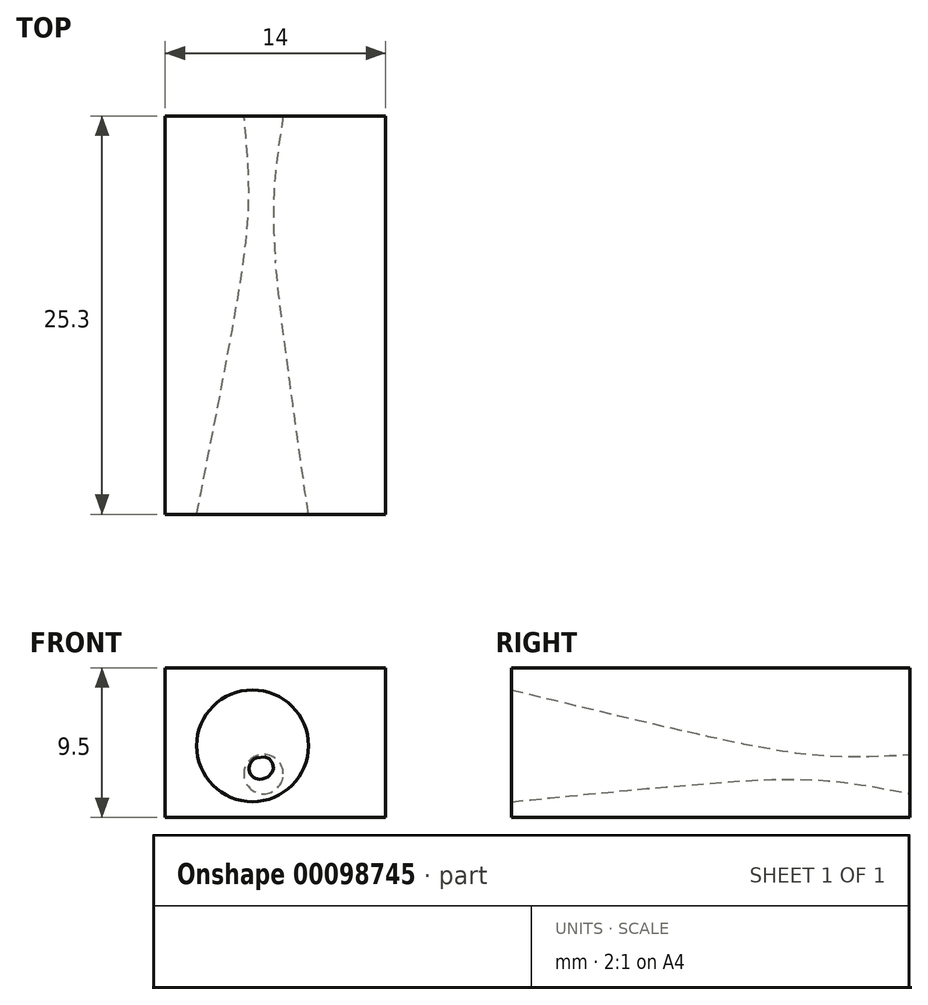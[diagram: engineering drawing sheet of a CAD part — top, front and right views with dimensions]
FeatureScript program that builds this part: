
annotation { "Feature Type Name" : "Feature", "Feature Type Description" : "" }
export const myFeature = defineFeature(function(context is Context, id is Id, definition is map)
    precondition{}
    {
        {
            var Q0;
            Q0=qCreatedBy(makeId("Front.planeOp"),FACE);
            var sketch = newSketch(context, id + "F0", { "sketchPlane" : qUnion([Q0])});
            skLineSegment(sketch, "E0.bottom", {"start": v(-0.64, 3.22) * mm, "end": v(13.36, 3.22) * mm});
            skLineSegment(sketch, "E0.top", {"start": v(-0.64, -6.28) * mm, "end": v(13.36, -6.28) * mm});
            skLineSegment(sketch, "E0.left", {"start": v(-0.64, 3.22) * mm, "end": v(-0.64, -6.28) * mm});
            skLineSegment(sketch, "E0.right", {"start": v(13.36, 3.22) * mm, "end": v(13.36, -6.28) * mm});
            skSolve(sketch);
        }
        {
            var Q0;
            Q0=makeQuery(id+"F0.imprint","IMPRINT",FACE,{"disambiguationData":[TD([[makeQuery(id+"F0.imprint","IMPRINT",EDGE,{"derivedFrom":sQuery(id+"F0.wireOp",EDGE,"E0.bottom")}),-1.0]])]});
            extrude(context, id + "F1", {"entities" : qUnion([Q0]), "oppositeDirection" : true, "depth" : 25.3 * mm});
        }
        {
            var Q0;
            Q0=makeQuery(id+"F1.opExtrude","CAP_FACE",FACE,{"disambiguationData":[OSD([sQuery(id+"F0.wireOp",EDGE,"E0.bottom"),sQuery(id+"F0.wireOp",EDGE,"E0.top"),sQuery(id+"F0.wireOp",EDGE,"E0.left"),sQuery(id+"F0.wireOp",EDGE,"E0.right")])],"isStart":true});
            var sketch = newSketch(context, id + "F2", { "sketchPlane" : qUnion([Q0])});
            skCircle(sketch, "E1", {"center": v(4.91, -1.73) * mm, "radius": 3.55 * mm});
            skSolve(sketch);
        }
        {
            var Q0;
            Q0=makeQuery(id+"F1.opExtrude","CAP_FACE",FACE,{"disambiguationData":[OSD([sQuery(id+"F0.wireOp",EDGE,"E0.bottom"),sQuery(id+"F0.wireOp",EDGE,"E0.top"),sQuery(id+"F0.wireOp",EDGE,"E0.left"),sQuery(id+"F0.wireOp",EDGE,"E0.right")])],"isStart":false});
            var sketch = newSketch(context, id + "F3", { "sketchPlane" : qUnion([Q0])});
            skCircle(sketch, "E2", {"center": v(-5.61, -3.53) * mm, "radius": 1.25 * mm});
            skSolve(sketch);
        }
        {
            var Q1;
            Q1=makeQuery(id+"F3.imprint","IMPRINT",FACE,{"disambiguationData":[TD([[makeQuery(id+"F3.imprint","IMPRINT",EDGE,{"derivedFrom":sQuery(id+"F3.wireOp",EDGE,"E2")}),1.0]])]});
            var Q2;
            Q2=makeQuery(id+"F2.imprint","IMPRINT",FACE,{"disambiguationData":[TD([[makeQuery(id+"F2.imprint","IMPRINT",EDGE,{"derivedFrom":sQuery(id+"F2.wireOp",EDGE,"E1")}),1.0]])]});
            loft(context, id + "F4", {"operationType" : NewBodyOperationType.REMOVE, "sheetProfilesArray" : [{ "sheetProfileEntities" : qUnion([Q1]) }, { "sheetProfileEntities" : qUnion([Q2]) }]});
        }
    });
